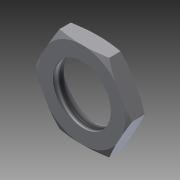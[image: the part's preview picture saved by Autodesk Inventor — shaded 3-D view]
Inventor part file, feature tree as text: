
AUTODESK INVENTOR PART (.ipt)
format: ipt  version: 2014 (Build 180170000, 170)  size: 131,584 bytes
history: native  units: in
note: dims shown in document units (in); Inventor stores cm internally (conversion verified against a paired STEP export)
features: other x7, sketch x3, revolve x1, extrude x1, hole x1
ambient origin geometry x8: Origin, YZ Plane, XZ Plane, XY Plane, X Axis, Y Axis, Z Axis, Center Point
bodies: Solid1 (feature_tree)
feature tree (13):
  revolve  "Revolution1"  [1 undecoded]
  extrude  "Extrusion1"  [1 undecoded]
  hole  "Drilling 1"  [1 undecoded]
  other  "nut_XY"
  other  "nut_YZ"
  other  "nut_ZX"
  other  "nut_X"
  other  "nut_Y"
  other  "nut_Z"
  other  "nut_Center"
  sketch  "Sketch_1"  dims[d0=360.0deg d1=0.118in d2=0.0in]
  sketch  "Sketch_2"  dims[d3=0.211in d4=0.059in d5=0.25in d6=0.25in d7=0.6184in d8=0.059in d9=0.0in]
  sketch  "Sketch3"
note: 3 required parameter values undecoded (feature->parameter linkage not recoverable at this tier; creation-order binding heuristic only, values carry confidence <= 0.55)